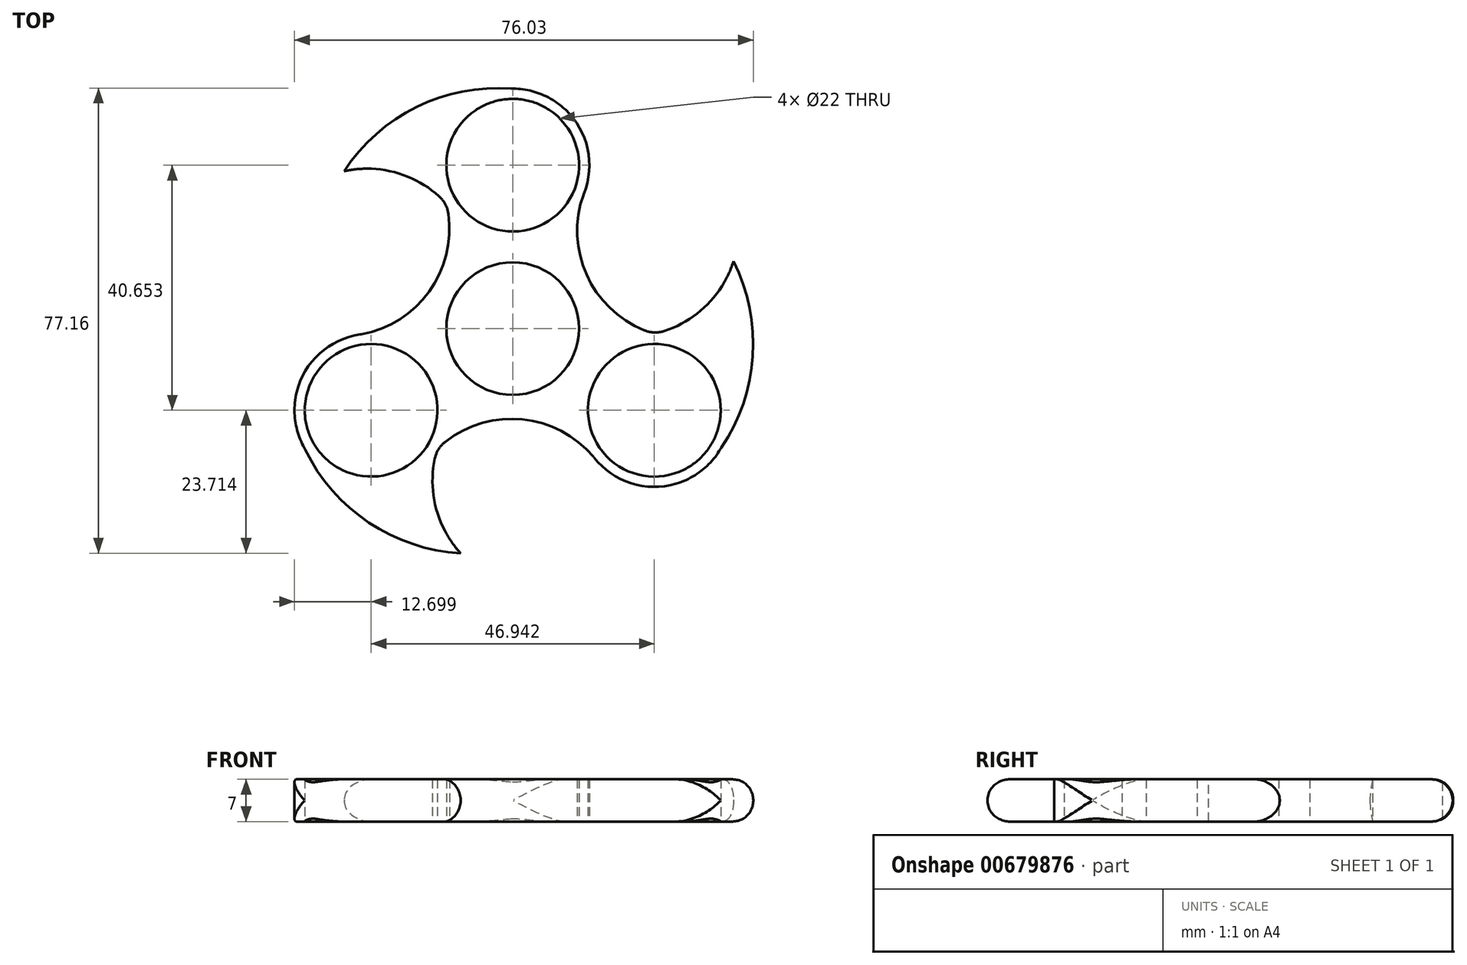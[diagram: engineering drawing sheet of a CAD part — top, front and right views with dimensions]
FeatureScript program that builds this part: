
annotation { "Feature Type Name" : "Feature", "Feature Type Description" : "" }
export const myFeature = defineFeature(function(context is Context, id is Id, definition is map)
    precondition{}
    {
        {
            var Q0;
            Q0=qCreatedBy(makeId("Top.planeOp"),FACE);
            var sketch = newSketch(context, id + "F0", { "sketchPlane" : qUnion([Q0])});
            skCircle(sketch, "E0", {"center": v(0, 40.4) * mm, "radius": 11 * mm});
            skCircle(sketch, "E1.1.0", {"center": v(-23.47, -0.25) * mm, "radius": 11 * mm});
            skCircle(sketch, "E1.2.0", {"center": v(23.47, -0.25) * mm, "radius": 11 * mm});
            skPoint(sketch, "E1.center", {"position": v(0, 13.3) * mm});
            skCircle(sketch, "E2", {"center": v(0, 13.3) * mm, "radius": 11 * mm});
            skCircle(sketch, "E3", {"center": v(0, 40.4) * mm, "radius": 12.7 * mm});
            skCircle(sketch, "E4.1.0", {"center": v(-23.47, -0.25) * mm, "radius": 12.7 * mm});
            skCircle(sketch, "E4.2.0", {"center": v(23.47, -0.25) * mm, "radius": 12.7 * mm});
            skArc(sketch, "E5", {"start": v(11.95, 36.1) * mm, "mid": v(12.48, 21.73) * mm, "end": v(23.47, 12.45) * mm});
            skArc(sketch, "E6.1.0", {"start": v(-25.72, 12.25) * mm, "mid": v(-13.54, 19.9) * mm, "end": v(-11, 34.06) * mm});
            skArc(sketch, "E6.2.0", {"start": v(13.77, -8.44) * mm, "mid": v(1.06, -1.72) * mm, "end": v(-12.47, -6.6) * mm});
            skArc(sketch, "E7", {"start": v(-11, 34.06) * mm, "mid": v(-18.76, 39) * mm, "end": v(-27.95, 39.41) * mm});
            skArc(sketch, "E8.1.0", {"start": v(-12.47, -6.6) * mm, "mid": v(-12.88, -15.8) * mm, "end": v(-8.63, -23.96) * mm});
            skArc(sketch, "E8.2.0", {"start": v(23.47, 12.45) * mm, "mid": v(31.64, 16.7) * mm, "end": v(36.59, 24.46) * mm});
            skArc(sketch, "E9", {"start": v(-35.8, -3.33) * mm, "mid": v(-25.37, -17.8) * mm, "end": v(-8.63, -23.96) * mm});
            skArc(sketch, "E10.1.0", {"start": v(32.3, -9.37) * mm, "mid": v(39.62, 6.89) * mm, "end": v(36.59, 24.46) * mm});
            skArc(sketch, "E10.2.0", {"start": v(3.49, 52.62) * mm, "mid": v(-14.25, 50.82) * mm, "end": v(-27.95, 39.41) * mm});
            skSolve(sketch);
        }
        {
            var Q0;
            Q0 = qSketchRegion(id + "F0", true);
            extrude(context, id + "F1", {"entities" : qUnion([Q0]), "depth" : 7 * mm, "offsetDistance" : 25.4 * mm});
        }
        {
            var Q0;
            Q0=makeQuery(id+"F1.opExtrude","SWEPT_EDGE",EDGE,{"disambiguationData":[OSD([sQuery(id+"F0.wireOp",EDGE,"E3"),sQuery(id+"F0.wireOp",EDGE,"E10.2.0")])]});
            var Q1;
            Q1=makeQuery(id+"F1.opExtrude","SWEPT_EDGE",EDGE,{"disambiguationData":[OSD([sQuery(id+"F0.wireOp",EDGE,"E4.2.0"),sQuery(id+"F0.wireOp",EDGE,"E10.1.0")])]});
            var Q2;
            Q2=makeQuery(id+"F1.opExtrude","SWEPT_EDGE",EDGE,{"disambiguationData":[OSD([sQuery(id+"F0.wireOp",EDGE,"E4.1.0"),sQuery(id+"F0.wireOp",EDGE,"E6.2.0"),sQuery(id+"F0.wireOp",EDGE,"E8.1.0")])]});
            var Q3;
            Q3=makeQuery(id+"F1.opExtrude","SWEPT_EDGE",EDGE,{"disambiguationData":[OSD([sQuery(id+"F0.wireOp",EDGE,"E4.2.0"),sQuery(id+"F0.wireOp",EDGE,"E5"),sQuery(id+"F0.wireOp",EDGE,"E8.2.0")])]});
            var Q4;
            Q4=makeQuery(id+"F1.opExtrude","SWEPT_EDGE",EDGE,{"disambiguationData":[OSD([sQuery(id+"F0.wireOp",EDGE,"E3"),sQuery(id+"F0.wireOp",EDGE,"E5")])]});
            var Q5;
            Q5=makeQuery(id+"F1.opExtrude","SWEPT_EDGE",EDGE,{"disambiguationData":[OSD([sQuery(id+"F0.wireOp",EDGE,"E3"),sQuery(id+"F0.wireOp",EDGE,"E6.1.0"),sQuery(id+"F0.wireOp",EDGE,"E7")])]});
            var Q6;
            Q6=makeQuery(id+"F1.opExtrude","SWEPT_EDGE",EDGE,{"disambiguationData":[OSD([sQuery(id+"F0.wireOp",EDGE,"E4.1.0"),sQuery(id+"F0.wireOp",EDGE,"E9")])]});
            var Q7;
            Q7=makeQuery(id+"F1.opExtrude","SWEPT_EDGE",EDGE,{"disambiguationData":[OSD([sQuery(id+"F0.wireOp",EDGE,"E4.2.0"),sQuery(id+"F0.wireOp",EDGE,"E6.2.0")])]});
            var Q8;
            Q8=makeQuery(id+"F1.opExtrude","SWEPT_EDGE",EDGE,{"disambiguationData":[OSD([sQuery(id+"F0.wireOp",EDGE,"E4.1.0"),sQuery(id+"F0.wireOp",EDGE,"E6.1.0")])]});
            fillet(context, id + "F2", {"entities" : qUnion([Q0, Q1, Q2, Q3, Q4, Q5, Q6, Q7, Q8]), "radius" : 4.83 * mm, "tangentPropagation" : true, "rho" : 0.5, "crossSection" : FilletCrossSection.CONIC, "allowEdgeOverflow" : false});
        }
        {
            var Q0;
            Q0=makeQuery(id+"F1.opExtrude","CAP_EDGE",EDGE,{"disambiguationData":[OSD([sQuery(id+"F0.wireOp",EDGE,"E10.1.0")])],"isStart":false});
            var Q1;
            Q1=makeQuery(id+"F1.opExtrude","CAP_EDGE",EDGE,{"disambiguationData":[OSD([sQuery(id+"F0.wireOp",EDGE,"E9")])],"isStart":false});
            var Q2;
            Q2=makeQuery(id+"F1.opExtrude","CAP_EDGE",EDGE,{"disambiguationData":[OSD([sQuery(id+"F0.wireOp",EDGE,"E10.2.0")])],"isStart":false});
            var Q3;
            Q3=makeQuery(id+"F1.opExtrude","CAP_EDGE",EDGE,{"disambiguationData":[OSD([sQuery(id+"F0.wireOp",EDGE,"E9")])],"isStart":true});
            var Q4;
            Q4=makeQuery(id+"F1.opExtrude","CAP_EDGE",EDGE,{"disambiguationData":[OSD([sQuery(id+"F0.wireOp",EDGE,"E10.1.0")])],"isStart":true});
            var Q5;
            Q5=makeQuery(id+"F1.opExtrude","CAP_EDGE",EDGE,{"disambiguationData":[OSD([sQuery(id+"F0.wireOp",EDGE,"E10.2.0")])],"isStart":true});
            fillet(context, id + "F3", {"entities" : qUnion([Q0, Q1, Q2, Q3, Q4, Q5]), "radius" : 3.43 * mm, "tangentPropagation" : true, "allowEdgeOverflow" : false});
        }
    });
